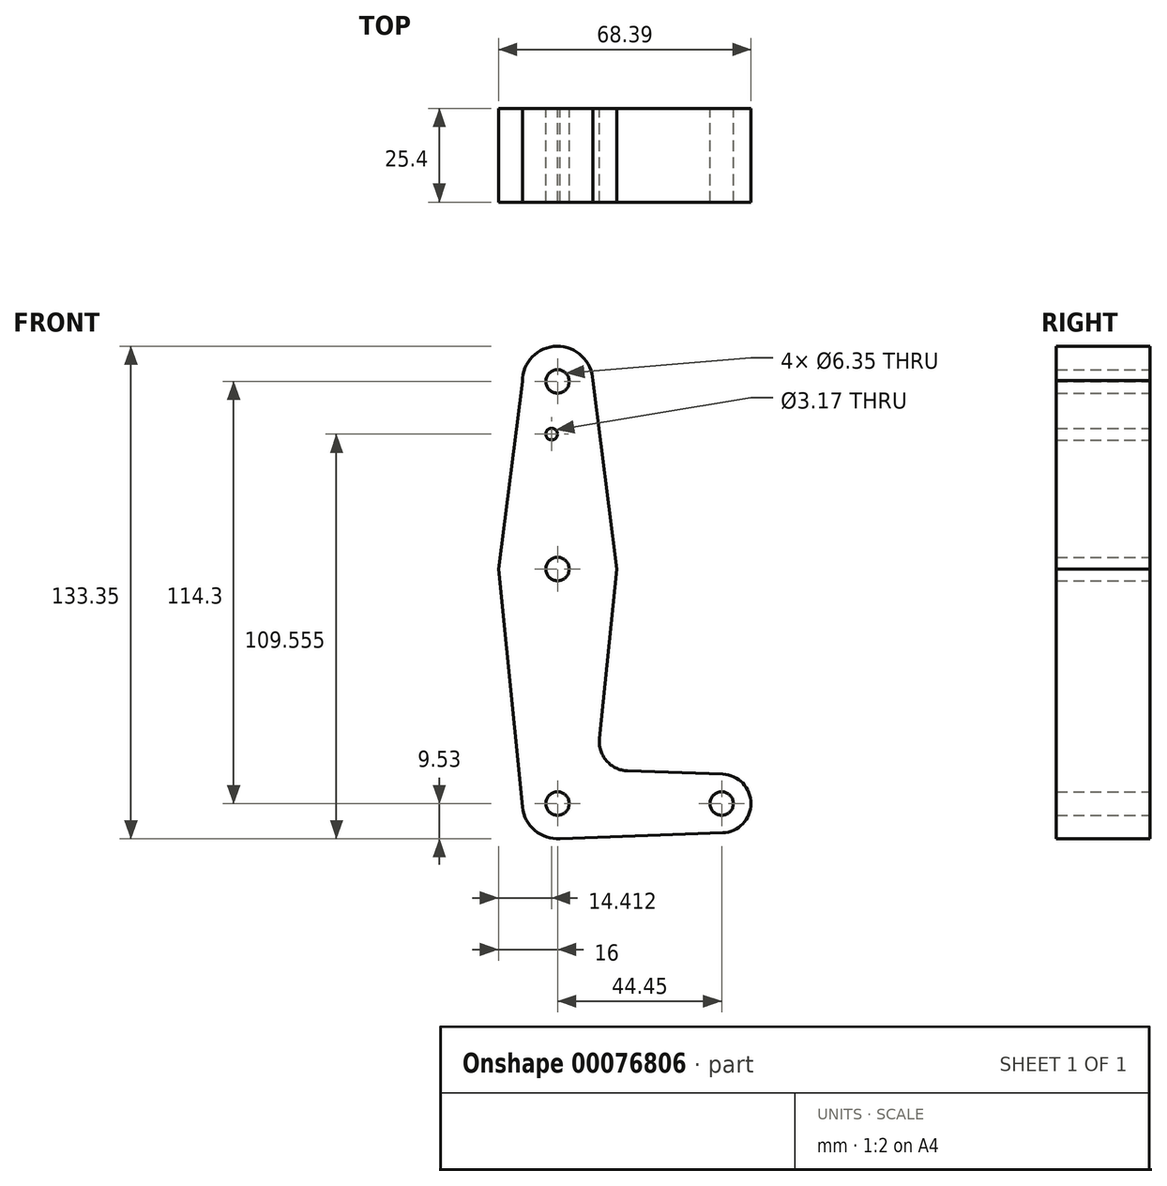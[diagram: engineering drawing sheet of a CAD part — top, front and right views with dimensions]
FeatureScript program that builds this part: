
annotation { "Feature Type Name" : "Feature", "Feature Type Description" : "" }
export const myFeature = defineFeature(function(context is Context, id is Id, definition is map)
    precondition{}
    {
        {
            var Q0;
            Q0=qCreatedBy(makeId("Front.planeOp"),FACE);
            var sketch = newSketch(context, id + "F0", { "sketchPlane" : qUnion([Q0])});
            skLineSegment(sketch, "E0", {"start": v(0, 0) * mm, "end": v(0, 50.8) * mm});
            skLineSegment(sketch, "E1", {"start": v(0, 0) * mm, "end": v(0, -63.5) * mm});
            skLineSegment(sketch, "E2", {"start": v(0, -63.5) * mm, "end": v(44.45, -63.5) * mm});
            skCircle(sketch, "E3", {"center": v(0, 50.8) * mm, "radius": 9.53 * mm});
            skCircle(sketch, "E4", {"center": v(0, 0) * mm, "radius": 15.88 * mm});
            skCircle(sketch, "E5", {"center": v(0, -63.5) * mm, "radius": 9.53 * mm});
            skCircle(sketch, "E6", {"center": v(44.45, -63.5) * mm, "radius": 7.94 * mm});
            skLineSegment(sketch, "E7", {"start": v(-9.52, 50.73) * mm, "end": v(-16, 0) * mm});
            skLineSegment(sketch, "E8", {"start": v(9.52, 51.04) * mm, "end": v(16, 0) * mm});
            skLineSegment(sketch, "E9", {"start": v(-16, 0) * mm, "end": v(-9.48, -64.46) * mm});
            skLineSegment(sketch, "E10", {"start": v(16, 0) * mm, "end": v(11.36, -45.9) * mm});
            skLineSegment(sketch, "E11", {"start": v(18.98, -54.65) * mm, "end": v(44.73, -55.57) * mm});
            skLineSegment(sketch, "E12", {"start": v(0, -73.03) * mm, "end": v(44.73, -71.43) * mm});
            skCircle(sketch, "E13", {"center": v(0, 50.8) * mm, "radius": 3.18 * mm});
            skCircle(sketch, "E14", {"center": v(0, 0) * mm, "radius": 3.18 * mm});
            skCircle(sketch, "E15", {"center": v(0, -63.5) * mm, "radius": 3.18 * mm});
            skCircle(sketch, "E16", {"center": v(44.45, -63.5) * mm, "radius": 3.18 * mm});
            skCircle(sketch, "E17", {"center": v(-1.59, 36.53) * mm, "radius": 1.59 * mm});
            skArc(sketch, "E18.filletArc", {"start": v(11.36, -45.9) * mm, "mid": v(13.27, -51.93) * mm, "end": v(18.98, -54.65) * mm});
            skSolve(sketch);
        }
        {
            var Q0;
            Q0 = qSketchRegion(id + "F0", true);
            var Q1;
            {var subQ0=sQuery(id+"F0.wireOp",EDGE,"E5");var subQ1=sQuery(id+"F0.wireOp",EDGE,"E1");var subQ2=makeQuery(id+"F0.imprint","INTERSECT",VERTEX,{"derivedFrom":[subQ1,subQ0]});Q1=makeQuery(id+"F0.imprint","IMPRINT",FACE,{"disambiguationData":[TD([[makeQuery(id+"F0.imprint","IMPRINT",EDGE,{"disambiguationData":[TD([[subQ2,-1.0]])],"derivedFrom":subQ1}),1.0]])]});}
            extrude(context, id + "F1", {"entities" : qUnion([Q0, Q1]), "depth" : 25.4 * mm});
        }
    });
